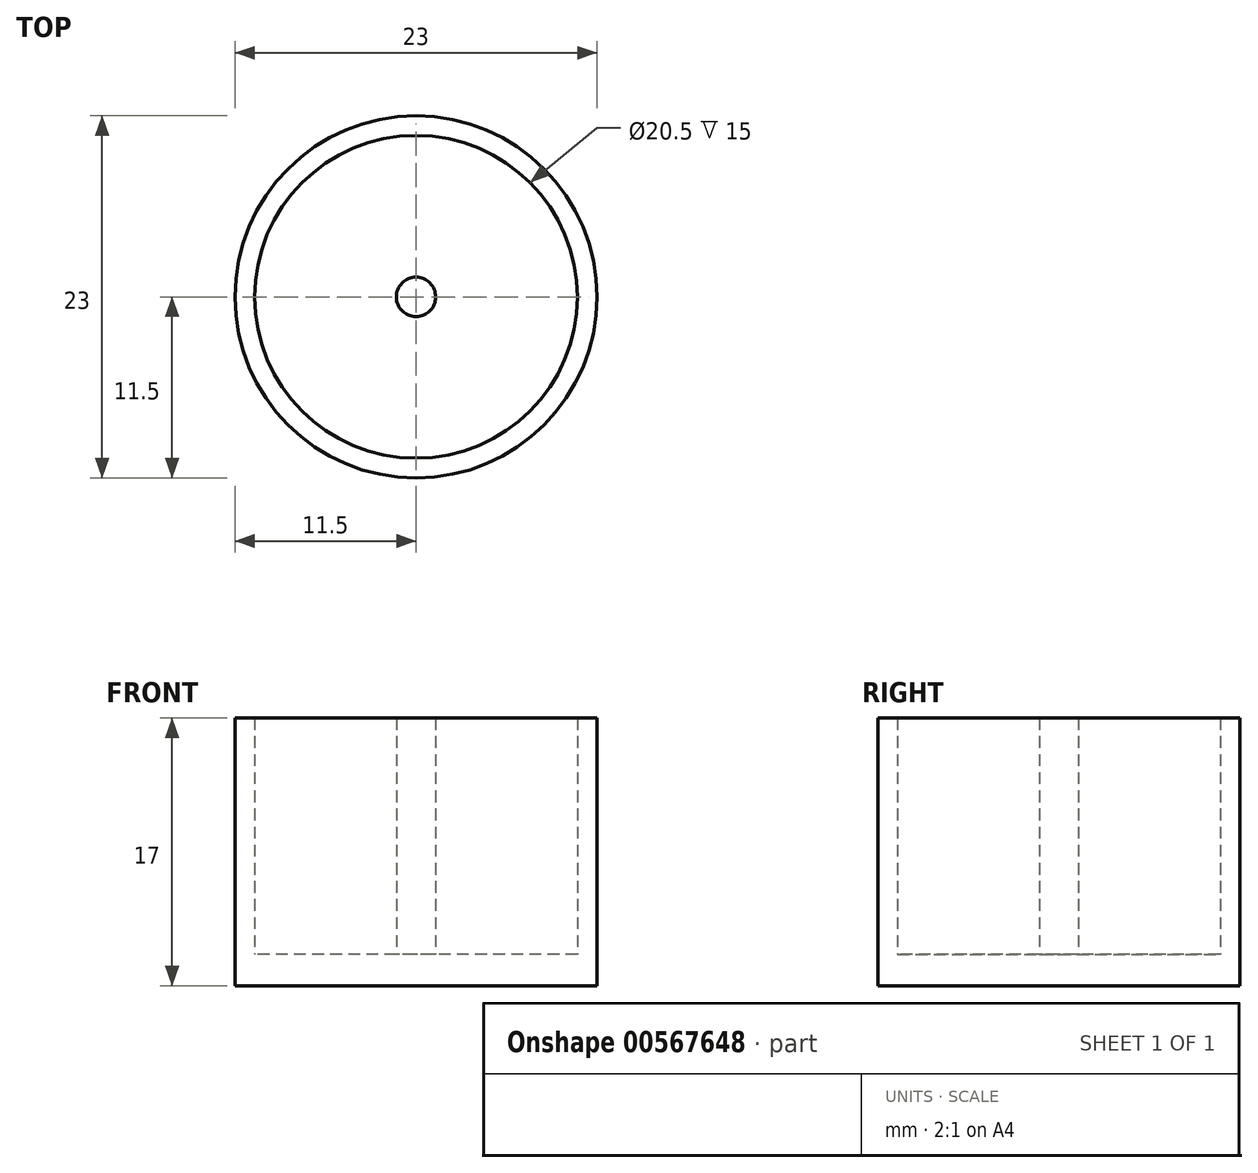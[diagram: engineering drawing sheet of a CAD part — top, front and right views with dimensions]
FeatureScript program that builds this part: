
annotation { "Feature Type Name" : "Feature", "Feature Type Description" : "" }
export const myFeature = defineFeature(function(context is Context, id is Id, definition is map)
    precondition{}
    {
        {
            var Q0;
            Q0=qCreatedBy(makeId("Top.planeOp"),FACE);
            var sketch = newSketch(context, id + "F0", { "sketchPlane" : qUnion([Q0])});
            skCircle(sketch, "E0", {"center": v(0, 0) * mm, "radius": 11.5 * mm});
            skSolve(sketch);
        }
        {
            var Q0;
            Q0 = qSketchRegion(id + "F0", true);
            extrude(context, id + "F1", {"entities" : qUnion([Q0]), "depth" : 2 * mm, "offsetDistance" : 25 * mm});
        }
        {
            var Q0;
            Q0=makeQuery(id+"F1.opExtrude","CAP_FACE",FACE,{"disambiguationData":[OSD([sQuery(id+"F0.wireOp",EDGE,"E0")])],"isStart":false});
            var sketch = newSketch(context, id + "F2", { "sketchPlane" : qUnion([Q0])});
            skCircle(sketch, "E1", {"center": v(0, 0) * mm, "radius": 11.5 * mm});
            skCircle(sketch, "E2", {"center": v(0, 0) * mm, "radius": 10.25 * mm});
            skSolve(sketch);
        }
        {
            var Q0;
            Q0 = qSketchRegion(id + "F2", true);
            extrude(context, id + "F3", {"entities" : qUnion([Q0]), "operationType" : NewBodyOperationType.ADD, "depth" : 15 * mm, "offsetDistance" : 25 * mm});
        }
        {
            var Q0;
            Q0=makeQuery(id+"F1.opExtrude","CAP_FACE",FACE,{"disambiguationData":[OSD([sQuery(id+"F0.wireOp",EDGE,"E0")])],"isStart":false});
            var sketch = newSketch(context, id + "F4", { "sketchPlane" : qUnion([Q0])});
            skCircle(sketch, "E3", {"center": v(0, 0) * mm, "radius": 1.25 * mm});
            skSolve(sketch);
        }
        {
            var Q0;
            Q0 = qSketchRegion(id + "F4", true);
            extrude(context, id + "F5", {"entities" : qUnion([Q0]), "operationType" : NewBodyOperationType.ADD, "depth" : 15 * mm, "offsetDistance" : 25 * mm});
        }
    });
